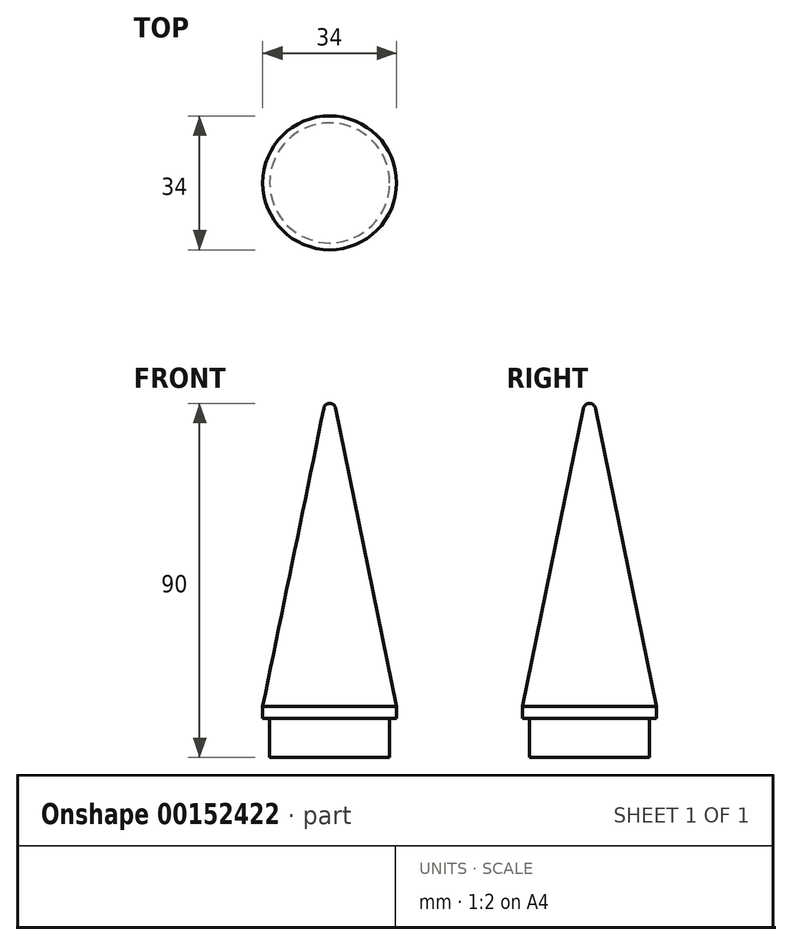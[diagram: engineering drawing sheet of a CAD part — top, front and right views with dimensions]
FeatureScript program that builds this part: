
annotation { "Feature Type Name" : "Feature", "Feature Type Description" : "" }
export const myFeature = defineFeature(function(context is Context, id is Id, definition is map)
    precondition{}
    {
        {
            var Q0;
            Q0=qCreatedBy(makeId("Top.planeOp"),FACE);
            cPlane(context, id + "F0", {"entities" : qUnion([Q0]), "cplaneType" : CPlaneType.OFFSET, "offset" : 337 * mm, "width" : 150 * mm, "height" : 150 * mm});
        }
        {
            var Q0;
            Q0=qCreatedBy(id+"F0.planeOp",FACE);
            var sketch = newSketch(context, id + "F1", { "sketchPlane" : qUnion([Q0])});
            skCircle(sketch, "E0", {"center": v(0, 0) * mm, "radius": 15.25 * mm});
            skSolve(sketch);
        }
        {
            var Q0;
            Q0=qSketchRegion(id+"F1",true);
            extrude(context, id + "F2", {"entities" : qUnion([Q0]), "oppositeDirection" : true, "depth" : 10 * mm});
        }
        {
            var Q0;
            Q0=qCreatedBy(id+"F0.planeOp",FACE);
            var sketch = newSketch(context, id + "F3", { "sketchPlane" : qUnion([Q0])});
            skPoint(sketch, "E1", {"position": v(-15.25, 0) * mm});
            skPoint(sketch, "E2", {"position": v(15.25, 0) * mm});
            skSolve(sketch);
        }
        {
            var Q0;
            Q0=qCreatedBy(makeId("Front.planeOp"),FACE);
            var sketch = newSketch(context, id + "F4", { "sketchPlane" : qUnion([Q0])});
            skLineSegment(sketch, "E3", {"start": v(0, 314.91) * mm, "end": v(0, 589.8) * mm, "construction": true});
            skLineSegment(sketch, "E4", {"start": v(-50.45, 417) * mm, "end": v(50.45, 417) * mm, "construction": true});
            skPoint(sketch, "E5", {"position": v(0, 417) * mm});
            skLineSegment(sketch, "E6", {"start": v(-0.8, 419.04) * mm, "end": v(-17, 340) * mm});
            skCircle(sketch, "E7", {"center": v(0, 415.5) * mm, "radius": 1.5 * mm});
            skLineSegment(sketch, "E8", {"start": v(0, 417) * mm, "end": v(0, 337) * mm});
            skLineSegment(sketch, "E9", {"start": v(-17, 314.91) * mm, "end": v(-17, 589.8) * mm, "construction": true});
            skPoint(sketch, "E10", {"position": v(-17, 340) * mm});
            skLineSegment(sketch, "E11", {"start": v(-17, 340) * mm, "end": v(-17, 337) * mm});
            skLineSegment(sketch, "E12", {"start": v(-17, 337) * mm, "end": v(0, 337) * mm});
            skSolve(sketch);
        }
        {
            var Q0;
            {var subQ0=sQuery(id+"F4.wireOp",EDGE,"E8");var subQ1=sQuery(id+"F4.wireOp",EDGE,"E7");var subQ2=makeQuery(id+"F4.imprint","INTERSECT",VERTEX,{"disambiguationData":[OD(0.0)],"derivedFrom":[subQ1,subQ0]});Q0=makeQuery(id+"F4.imprint","IMPRINT",FACE,{"disambiguationData":[TD([[makeQuery(id+"F4.imprint","IMPRINT",EDGE,{"disambiguationData":[TD([[subQ2,-1.0]])],"derivedFrom":subQ1}),1.0]])]});}
            var Q1;
            {var subQ0=sQuery(id+"F4.wireOp",EDGE,"E11");Q1=makeQuery(id+"F4.imprint","IMPRINT",FACE,{"disambiguationData":[TD([[makeQuery(id+"F4.imprint","IMPRINT",EDGE,{"derivedFrom":subQ0}),1.0]])]});}
            var Q2;
            Q2=sQuery(id+"F4.wireOp",EDGE,"E3");
            revolve(context, id + "F5", {"operationType" : NewBodyOperationType.ADD, "entities" : qUnion([Q0, Q1]), "axis" : qUnion([Q2]), "revolveType" : RevolveType.FULL});
        }
    });
